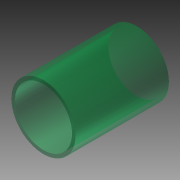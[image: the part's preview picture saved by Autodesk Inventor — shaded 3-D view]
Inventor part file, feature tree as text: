
AUTODESK INVENTOR PART (.ipt)
format: ipt  version: 2011 (Build 150229000, 229)  size: 92,160 bytes
history: native  units: mm (DEFAULTED — no unit token found)
features: extrude x1, sketch x1
ambient origin geometry x8: Origin, YZ Plane, XZ Plane, XY Plane, X Axis, Y Axis, Z Axis, Center Point
feature tree (2):
  extrude  "Extrusion1"  Depth=41.0mm
  sketch  "Sketch1"  dims[d0=46.0mm d1=41.0mm d2=67.0mm d3=0.0mm]
